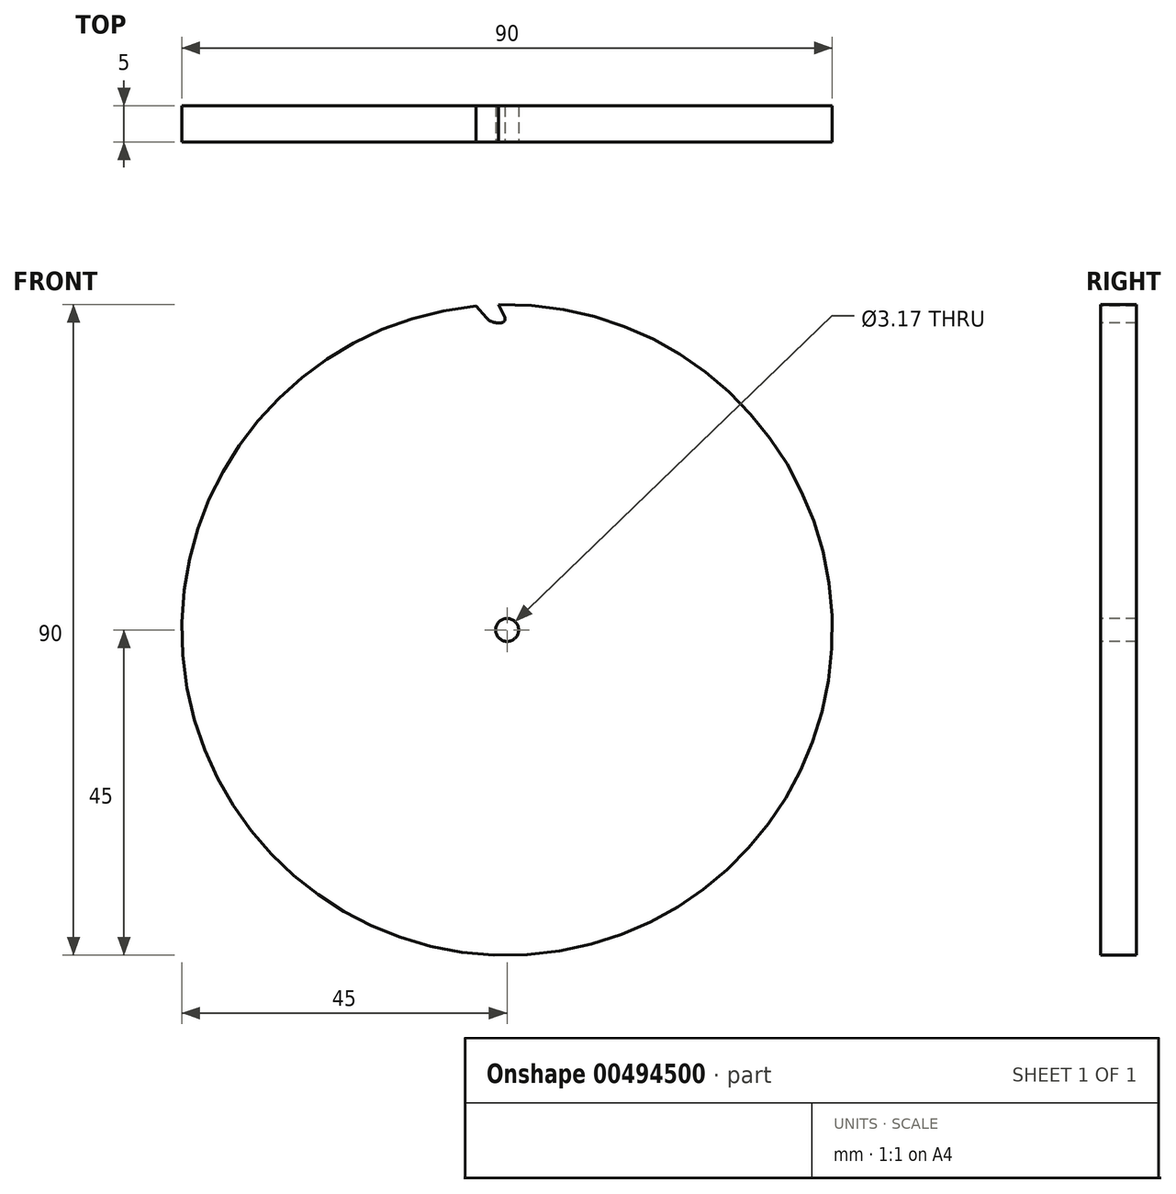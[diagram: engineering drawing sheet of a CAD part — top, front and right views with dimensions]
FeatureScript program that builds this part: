
annotation { "Feature Type Name" : "Feature", "Feature Type Description" : "" }
export const myFeature = defineFeature(function(context is Context, id is Id, definition is map)
    precondition{}
    {
        {
            var Q0;
            Q0=qCreatedBy(makeId("Front.planeOp"),FACE);
            var sketch = newSketch(context, id + "F0", { "sketchPlane" : qUnion([Q0])});
            skCircle(sketch, "E0", {"center": v(0, 0) * mm, "radius": 45 * mm});
            skSolve(sketch);
        }
        {
            var Q0;
            Q0=qSketchRegion(id+"F0",true);
            extrude(context, id + "F1", {"entities" : qUnion([Q0]), "depth" : 5 * mm, "offsetDistance" : 25 * mm});
        }
        {
            var Q0;
            Q0=makeQuery(id+"F1.opExtrude","CAP_FACE",FACE,{"disambiguationData":[OSD([sQuery(id+"F0.wireOp",EDGE,"E0")])],"isStart":false});
            var sketch = newSketch(context, id + "F2", { "sketchPlane" : qUnion([Q0])});
            skCircle(sketch, "E1", {"center": v(0, 0) * mm, "radius": 42.5 * mm});
            skLineSegment(sketch, "E2", {"start": v(0, 42.5) * mm, "end": v(-1.18, 44.98) * mm});
            skLineSegment(sketch, "E3", {"start": v(0.4, 45) * mm, "end": v(2.22, 42.44) * mm});
            skLineSegment(sketch, "E4", {"start": v(0, 42.5) * mm, "end": v(0, 0) * mm, "construction": true});
            skLineSegment(sketch, "E5", {"start": v(0, 0) * mm, "end": v(2.22, 42.44) * mm, "construction": true});
            skLineSegment(sketch, "E6", {"start": v(-2.22, 42.44) * mm, "end": v(-4.31, 44.8) * mm});
            skLineSegment(sketch, "E7", {"start": v(-1.18, 44.98) * mm, "end": v(0, 0) * mm, "construction": true});
            skLineSegment(sketch, "E8", {"start": v(0.4, 45) * mm, "end": v(0, 0) * mm, "construction": true});
            skLineSegment(sketch, "E9", {"start": v(-4.31, 44.8) * mm, "end": v(0, 0) * mm, "construction": true});
            skLineSegment(sketch, "E10", {"start": v(-2.22, 42.44) * mm, "end": v(0, 0) * mm, "construction": true});
            skSolve(sketch);
        }
        {
            var Q0;
            Q0=makeQuery(id+"F1.opExtrude","CAP_FACE",FACE,{"disambiguationData":[OSD([sQuery(id+"F0.wireOp",EDGE,"E0")])],"isStart":false});
            var sketch = newSketch(context, id + "F3", { "sketchPlane" : qUnion([Q0])});
            skCircle(sketch, "E11", {"center": v(0, 0) * mm, "radius": 22.93 * mm});
            skSolve(sketch);
        }
        {
            var Q0;
            {var subQ0=sQuery(id+"F2.wireOp",EDGE,"E2");Q0=makeQuery(id+"F2.imprint","IMPRINT",FACE,{"disambiguationData":[TD([[makeQuery(id+"F2.imprint","IMPRINT",EDGE,{"derivedFrom":subQ0}),1.0]])]});}
            extrude(context, id + "F4", {"entities" : qUnion([Q0]), "operationType" : NewBodyOperationType.REMOVE, "oppositeDirection" : true, "depth" : 25 * mm, "offsetDistance" : 25 * mm});
        }
        {
            var Q0;
            Q0=makeQuery(id+"F4.boolean.opBoolean","COPY",EDGE,{"derivedFrom":makeQuery(id+"F4.opExtrude","SWEPT_EDGE",EDGE,{"disambiguationData":[OSD([sQuery(id+"F0.wireOp",EDGE,"E0"),sQuery(id+"F2.wireOp",EDGE,"E6")])]})});
            var Q1;
            Q1=makeQuery(id+"F4.boolean.opBoolean","COPY",EDGE,{"derivedFrom":makeQuery(id+"F4.opExtrude","SWEPT_EDGE",EDGE,{"disambiguationData":[OSD([sQuery(id+"F2.wireOp",EDGE,"E1"),sQuery(id+"F2.wireOp",EDGE,"E6")])]})});
            fillet(context, id + "F5", {"entities" : qUnion([Q0, Q1]), "radius" : 2 * mm, "tangentPropagation" : true, "allowEdgeOverflow" : false});
        }
        {
            var Q0;
            Q0=makeQuery(id+"F4.boolean.opBoolean","COPY",EDGE,{"derivedFrom":makeQuery(id+"F4.opExtrude","SWEPT_EDGE",EDGE,{"disambiguationData":[OSD([sQuery(id+"F2.wireOp",EDGE,"E1"),sQuery(id+"F2.wireOp",EDGE,"E2")])]})});
            fillet(context, id + "F6", {"entities" : qUnion([Q0]), "radius" : 0.5 * mm, "tangentPropagation" : true, "allowEdgeOverflow" : false});
        }
        {
            var Q0;
            Q0=makeQuery(id+"F1.opExtrude","CAP_FACE",FACE,{"disambiguationData":[OSD([sQuery(id+"F0.wireOp",EDGE,"E0")])],"isStart":false});
            var sketch = newSketch(context, id + "F7", { "sketchPlane" : qUnion([Q0])});
            skCircle(sketch, "E12", {"center": v(0, 0) * mm, "radius": 1.59 * mm});
            skSolve(sketch);
        }
        {
            var Q0;
            Q0 = qSketchRegion(id + "F7", true);
            extrude(context, id + "F8", {"entities" : qUnion([Q0]), "operationType" : NewBodyOperationType.REMOVE, "oppositeDirection" : true, "depth" : 25 * mm, "offsetDistance" : 25 * mm});
        }
    });
